# Revit family: CR154BR
name_source: partatom
category: Aparatos eléctricos
revit_build: Autodesk Revit 2016 (Build: 20150220_1215(x64)
units: mm (PartAtom-declared; Revit-internal decimal feet)

## family parameters
Anfitrión = Cara
Compartido = No
Corte con vacíos al cargar = No
Cota de conector redondo = Diámetro de uso
Mantener orientación de anotación = No
Número OmniClass = 23.80.50.11.11
Punto de cálculo de habitación = No
Tipo de pieza = Normal
Título OmniClass = Receptacle Terminal Units

## types (1)
- Módulo /6 - Grafito
    Acabado = Grafito RAL7021
    CRXX (AltoxLargoxAncho) = 45 x 130 x 190 mm
    Capacidad = 1-12 conectores CR
    Carga eléctrica = Potencia
    Compatibilidad = Gama CR
    Composición = Cubeta, Laterales (4ud), Tapa, Tornillería tapa + montaje en suelo (2x4ud), Conectores CR, Cableado interno en línea 2,5mm
    Código de montaje = D5020100
    Descripción = Caja de conexiones tipo CR
    Elevación por defecto = 1200 mm
    Fabricante = MMCONECTA
    Factor de potencia = 1
    Instalación = Suelo / Techo
    Materia prima = Policarbonato libre de halógenos
    Modelo = CR15BR
    Normativas = UNE 20451:1997 / Marcado CE
    Polos = 1
    Potencia aparente = 3500 W
    URL = http://www.mmconecta.com
    Voltaje = 250 V

## geometry (parser evidence)
native form markers: Blend x4
no freeform markers — native parametric forms only
